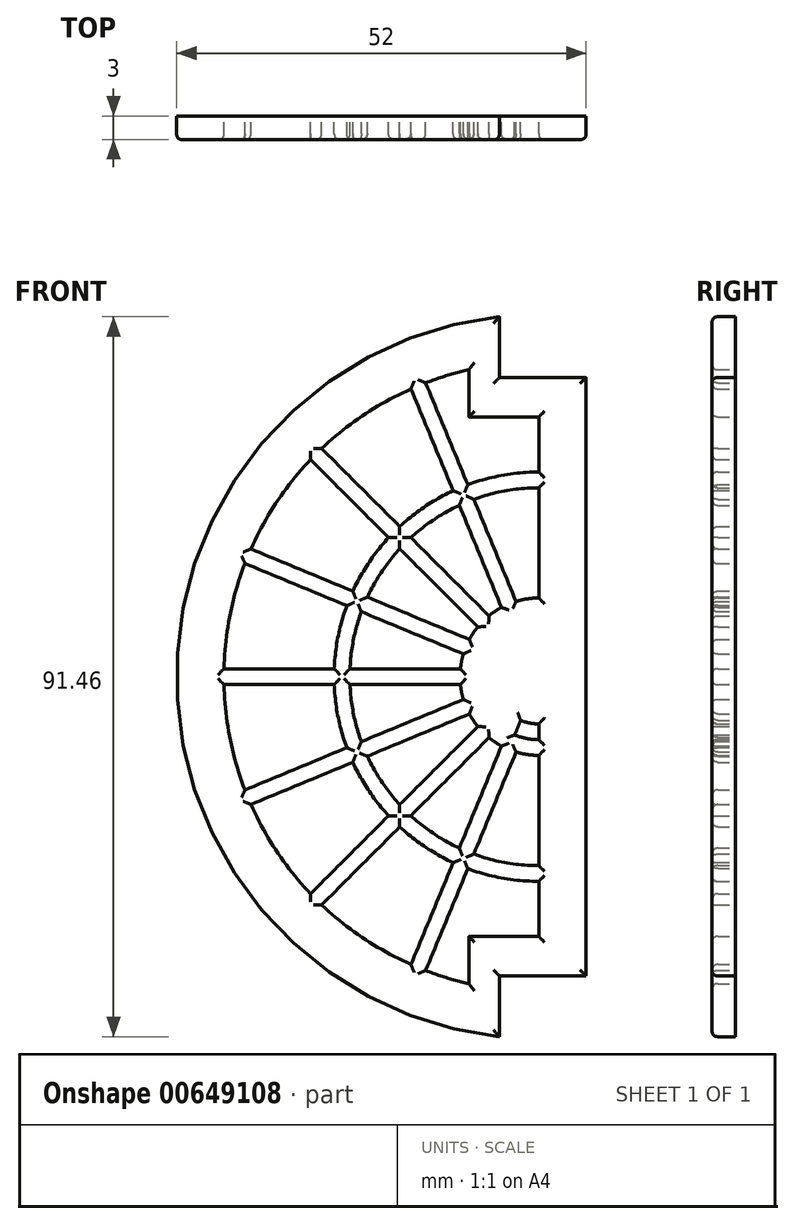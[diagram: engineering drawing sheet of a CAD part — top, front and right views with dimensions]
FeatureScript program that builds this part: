
annotation { "Feature Type Name" : "Feature", "Feature Type Description" : "" }
export const myFeature = defineFeature(function(context is Context, id is Id, definition is map)
    precondition{}
    {
        {
            var Q0;
            Q0=qCreatedBy(makeId("Front.planeOp"),FACE);
            var sketch = newSketch(context, id + "F0", { "sketchPlane" : qUnion([Q0])});
            skPoint(sketch, "E0", {"position": v(0, 0) * mm});
            skPoint(sketch, "E1", {"position": v(-24, 0) * mm});
            skPoint(sketch, "E2", {"position": v(-26, 0) * mm});
            skPoint(sketch, "E3", {"position": v(-28.28, 28.28) * mm});
            skPoint(sketch, "E4", {"position": v(-36.96, 15.3) * mm});
            skPoint(sketch, "E5", {"position": v(-36.96, -15.3) * mm});
            skPoint(sketch, "E6", {"position": v(-28.28, -28.28) * mm});
            skPoint(sketch, "E7", {"position": v(-15.3, -36.96) * mm});
            skPoint(sketch, "E8", {"position": v(-15.3, 36.96) * mm});
            skPoint(sketch, "E9", {"position": v(0, 26) * mm});
            skPoint(sketch, "E10", {"position": v(-9.95, 24.02) * mm});
            skPoint(sketch, "E11", {"position": v(-18.38, 18.38) * mm});
            skPoint(sketch, "E12", {"position": v(-24.02, 9.95) * mm});
            skPoint(sketch, "E13", {"position": v(-22.17, 9.18) * mm});
            skPoint(sketch, "E14", {"position": v(-16.97, 16.97) * mm});
            skPoint(sketch, "E15", {"position": v(-9.18, 22.17) * mm});
            skPoint(sketch, "E16", {"position": v(0, 24) * mm});
            skPoint(sketch, "E17", {"position": v(-22.17, -9.18) * mm});
            skPoint(sketch, "E18", {"position": v(-24.02, -9.95) * mm});
            skPoint(sketch, "E19", {"position": v(-16.97, -16.97) * mm});
            skPoint(sketch, "E20", {"position": v(-18.38, -18.38) * mm});
            skPoint(sketch, "E21", {"position": v(-9.18, -22.17) * mm});
            skPoint(sketch, "E22", {"position": v(-9.95, -24.02) * mm});
            skPoint(sketch, "E23", {"position": v(0, -24) * mm});
            skPoint(sketch, "E24", {"position": v(0, -26) * mm});
            skPoint(sketch, "E25", {"position": v(-40, 0) * mm});
            skPoint(sketch, "E26", {"position": v(6, -38) * mm});
            skLineSegment(sketch, "E27", {"start": v(-5, -38) * mm, "end": v(-5, -45.73) * mm});
            skLineSegment(sketch, "E28", {"start": v(-15.3, 36.96) * mm, "end": v(-9.95, 24.02) * mm});
            skLineSegment(sketch, "E29", {"start": v(-9.18, 22.17) * mm, "end": v(0, 0) * mm});
            skLineSegment(sketch, "E30", {"start": v(-28.28, 28.28) * mm, "end": v(-18.38, 18.38) * mm});
            skLineSegment(sketch, "E31", {"start": v(-16.97, 16.97) * mm, "end": v(0, 0) * mm});
            skLineSegment(sketch, "E32", {"start": v(-36.96, 15.3) * mm, "end": v(-24.02, 9.95) * mm});
            skLineSegment(sketch, "E33", {"start": v(-22.17, 9.18) * mm, "end": v(0, 0) * mm});
            skLineSegment(sketch, "E34", {"start": v(-40, 0) * mm, "end": v(-26, 0) * mm});
            skLineSegment(sketch, "E35", {"start": v(-24, 0) * mm, "end": v(0, 0) * mm});
            skLineSegment(sketch, "E36", {"start": v(-36.96, -15.3) * mm, "end": v(-24.02, -9.95) * mm});
            skLineSegment(sketch, "E37", {"start": v(-22.17, -9.18) * mm, "end": v(0, 0) * mm});
            skLineSegment(sketch, "E38", {"start": v(-28.28, -28.28) * mm, "end": v(-18.38, -18.38) * mm});
            skLineSegment(sketch, "E39", {"start": v(-16.97, -16.97) * mm, "end": v(0, 0) * mm});
            skLineSegment(sketch, "E40", {"start": v(-15.3, -36.96) * mm, "end": v(-9.95, -24.02) * mm});
            skLineSegment(sketch, "E41", {"start": v(-9.18, -22.17) * mm, "end": v(0, 0) * mm});
            skArc(sketch, "E42", {"start": v(-46, 0) * mm, "mid": v(-34.25, -30.7) * mm, "end": v(-5, -45.73) * mm});
            skArc(sketch, "E43", {"start": v(0, 26) * mm, "mid": v(-18.38, 18.38) * mm, "end": v(-26, 0) * mm});
            skArc(sketch, "E44", {"start": v(-26, 0) * mm, "mid": v(-18.38, -18.38) * mm, "end": v(0, -26) * mm});
            skArc(sketch, "E45", {"start": v(0, 24) * mm, "mid": v(-24, 0) * mm, "end": v(0, -24) * mm});
            skArc(sketch, "E46", {"start": v(0, 10) * mm, "mid": v(-10, 0) * mm, "end": v(0, -10) * mm});
            skArc(sketch, "E47", {"start": v(0, 8) * mm, "mid": v(-8, 0) * mm, "end": v(0, -8) * mm});
            skLineSegment(sketch, "E48", {"start": v(6, 38) * mm, "end": v(6, -38) * mm});
            skLineSegment(sketch, "E49", {"start": v(0, 24) * mm, "end": v(0, 10) * mm});
            skLineSegment(sketch, "E50", {"start": v(0, 8) * mm, "end": v(0, -8) * mm});
            skLineSegment(sketch, "E51", {"start": v(0, -10) * mm, "end": v(0, -24) * mm});
            skLineSegment(sketch, "E52", {"start": v(6, -38) * mm, "end": v(-5, -38) * mm});
            skPoint(sketch, "E53", {"position": v(-5, 45.73) * mm});
            skArc(sketch, "E54", {"start": v(-5, 45.73) * mm, "mid": v(-34.25, 30.7) * mm, "end": v(-46, 0) * mm});
            skLineSegment(sketch, "E55", {"start": v(6, 38) * mm, "end": v(-5, 38) * mm});
            skPoint(sketch, "E56", {"position": v(0, 33) * mm});
            skLineSegment(sketch, "E57", {"start": v(0, 33) * mm, "end": v(-8.89, 33) * mm});
            skPoint(sketch, "E58", {"position": v(-8.89, 39) * mm});
            skArc(sketch, "E59", {"start": v(-8.89, 39) * mm, "mid": v(-31.27, 24.94) * mm, "end": v(-40, 0) * mm});
            skLineSegment(sketch, "E60", {"start": v(0, 33) * mm, "end": v(0, 26) * mm});
            skPoint(sketch, "E61", {"position": v(-5, -45.73) * mm});
            skLineSegment(sketch, "E62", {"start": v(-8.89, -33) * mm, "end": v(0, -33) * mm});
            skLineSegment(sketch, "E63", {"start": v(0, -26) * mm, "end": v(0, -33) * mm});
            skPoint(sketch, "E64", {"position": v(-8.89, -39) * mm});
            skPoint(sketch, "E65", {"position": v(-8.89, -33) * mm});
            skArc(sketch, "E66", {"start": v(-40, 0) * mm, "mid": v(-31.27, -24.94) * mm, "end": v(-8.89, -39) * mm});
            skLineSegment(sketch, "E67", {"start": v(-8.89, -33) * mm, "end": v(-8.89, -39) * mm});
            skLineSegment(sketch, "E68", {"start": v(-8.89, 39) * mm, "end": v(-8.89, 33) * mm});
            skLineSegment(sketch, "E69", {"start": v(-5, 45.73) * mm, "end": v(-5, 38) * mm});
            skLineSegment(sketch, "E70.0", {"start": v(-39.99, -1) * mm, "end": v(-25.98, -1) * mm});
            skLineSegment(sketch, "E71.0", {"start": v(-39.99, 1) * mm, "end": v(-25.98, 1) * mm});
            skLineSegment(sketch, "E72", {"start": v(-23.98, -1) * mm, "end": v(-9.95, -1) * mm});
            skLineSegment(sketch, "E73", {"start": v(-23.98, 1) * mm, "end": v(-9.95, 1) * mm});
            skLineSegment(sketch, "E74.0", {"start": v(-36.56, -16.23) * mm, "end": v(-23.62, -10.87) * mm});
            skLineSegment(sketch, "E75.0", {"start": v(-37.33, -14.38) * mm, "end": v(-24.39, -9.02) * mm});
            skPoint(sketch, "E76", {"position": v(-21.77, 10.1) * mm});
            skPoint(sketch, "E77", {"position": v(-8.8, 4.73) * mm});
            skPoint(sketch, "E78", {"position": v(-9.58, 2.88) * mm});
            skPoint(sketch, "E79", {"position": v(-22.54, 8.25) * mm});
            skLineSegment(sketch, "E80", {"start": v(-8.8, 4.73) * mm, "end": v(-21.77, 10.1) * mm});
            skLineSegment(sketch, "E81", {"start": v(-9.58, 2.88) * mm, "end": v(-22.54, 8.25) * mm});
            skPoint(sketch, "E82", {"position": v(-9.57, -2.88) * mm});
            skPoint(sketch, "E83", {"position": v(-9.24, -3.83) * mm});
            skPoint(sketch, "E84", {"position": v(-7.07, -7.07) * mm});
            skPoint(sketch, "E85", {"position": v(-7.74, -6.33) * mm});
            skPoint(sketch, "E86", {"position": v(-6.33, -7.74) * mm});
            skPoint(sketch, "E87", {"position": v(-4.73, -8.8) * mm});
            skPoint(sketch, "E88", {"position": v(-2.88, -9.58) * mm});
            skPoint(sketch, "E89", {"position": v(-7.07, 7.07) * mm});
            skPoint(sketch, "E90", {"position": v(-7.74, 6.33) * mm});
            skPoint(sketch, "E91", {"position": v(-6.33, 7.74) * mm});
            skPoint(sketch, "E92", {"position": v(-4.73, 8.8) * mm});
            skPoint(sketch, "E93", {"position": v(-2.88, 9.57) * mm});
            skPoint(sketch, "E94", {"position": v(-22.54, -8.25) * mm});
            skPoint(sketch, "E95", {"position": v(-17.66, -16.25) * mm});
            skPoint(sketch, "E96", {"position": v(-16.25, -17.66) * mm});
            skPoint(sketch, "E97", {"position": v(-10.1, -21.77) * mm});
            skPoint(sketch, "E98", {"position": v(-8.25, -22.54) * mm});
            skPoint(sketch, "E99", {"position": v(-14.38, -37.33) * mm});
            skPoint(sketch, "E100", {"position": v(-27.57, -28.98) * mm});
            skPoint(sketch, "E101", {"position": v(-28.98, -27.57) * mm});
            skPoint(sketch, "E102", {"position": v(-23.62, 10.87) * mm});
            skPoint(sketch, "E103", {"position": v(-24.39, 9.02) * mm});
            skPoint(sketch, "E104", {"position": v(-36.56, 16.23) * mm});
            skPoint(sketch, "E105", {"position": v(-37.33, 14.38) * mm});
            skPoint(sketch, "E106", {"position": v(-19.08, 17.66) * mm});
            skPoint(sketch, "E107", {"position": v(-8.25, 22.54) * mm});
            skPoint(sketch, "E108", {"position": v(-10.1, 21.77) * mm});
            skPoint(sketch, "E109", {"position": v(-10.87, 23.62) * mm});
            skPoint(sketch, "E110", {"position": v(-14.38, 37.33) * mm});
            skPoint(sketch, "E111", {"position": v(-16.23, 36.56) * mm});
            skPoint(sketch, "E112", {"position": v(-27.57, 28.98) * mm});
            skPoint(sketch, "E113", {"position": v(-28.98, 27.57) * mm});
            skLineSegment(sketch, "E114", {"start": v(-16.23, 36.56) * mm, "end": v(-10.87, 23.62) * mm});
            skLineSegment(sketch, "E115", {"start": v(-28.98, 27.57) * mm, "end": v(-19.08, 17.66) * mm});
            skLineSegment(sketch, "E116", {"start": v(-36.56, 16.23) * mm, "end": v(-23.62, 10.87) * mm});
            skLineSegment(sketch, "E117", {"start": v(-37.33, 14.38) * mm, "end": v(-24.39, 9.02) * mm});
            skLineSegment(sketch, "E118", {"start": v(-8.25, 22.54) * mm, "end": v(-2.88, 9.57) * mm});
            skLineSegment(sketch, "E119", {"start": v(-10.1, 21.77) * mm, "end": v(-4.73, 8.8) * mm});
            skLineSegment(sketch, "E120", {"start": v(-9.57, -2.88) * mm, "end": v(-22.54, -8.25) * mm});
            skLineSegment(sketch, "E121", {"start": v(-2.88, -9.58) * mm, "end": v(-8.25, -22.54) * mm});
            skLineSegment(sketch, "E122", {"start": v(-4.73, -8.8) * mm, "end": v(-10.1, -21.77) * mm});
            skLineSegment(sketch, "E123", {"start": v(-6.33, -7.74) * mm, "end": v(-16.25, -17.66) * mm});
            skLineSegment(sketch, "E124", {"start": v(-7.74, -6.33) * mm, "end": v(-17.66, -16.25) * mm});
            skPoint(sketch, "E125", {"position": v(-8.81, -4.73) * mm});
            skPoint(sketch, "E126", {"position": v(-17.66, -19.08) * mm});
            skPoint(sketch, "E127", {"position": v(-19.08, -17.66) * mm});
            skLineSegment(sketch, "E128", {"start": v(-19.08, -17.66) * mm, "end": v(-28.98, -27.57) * mm});
            skLineSegment(sketch, "E129", {"start": v(-17.66, -19.08) * mm, "end": v(-27.57, -28.98) * mm});
            skPoint(sketch, "E130", {"position": v(-3.83, 9.24) * mm});
            skPoint(sketch, "E131", {"position": v(-9.02, -24.39) * mm});
            skLineSegment(sketch, "E132", {"start": v(-9.02, -24.39) * mm, "end": v(-14.38, -37.33) * mm});
            skPoint(sketch, "E133", {"position": v(-9.02, 24.39) * mm});
            skLineSegment(sketch, "E134", {"start": v(-14.38, 37.33) * mm, "end": v(-9.02, 24.39) * mm});
            skPoint(sketch, "E135", {"position": v(-17.66, 19.08) * mm});
            skLineSegment(sketch, "E136", {"start": v(-17.66, 19.08) * mm, "end": v(-27.57, 28.98) * mm});
            skPoint(sketch, "E137", {"position": v(-16.25, 17.66) * mm});
            skPoint(sketch, "E138", {"position": v(-17.66, 16.25) * mm});
            skLineSegment(sketch, "E139", {"start": v(-16.25, 17.66) * mm, "end": v(-6.33, 7.74) * mm});
            skLineSegment(sketch, "E140", {"start": v(-17.66, 16.25) * mm, "end": v(-7.74, 6.33) * mm});
            skPoint(sketch, "E141", {"position": v(-21.77, -10.1) * mm});
            skLineSegment(sketch, "E142", {"start": v(-8.81, -4.73) * mm, "end": v(-21.77, -10.1) * mm});
            skPoint(sketch, "E143", {"position": v(-16.23, -36.56) * mm});
            skPoint(sketch, "E144", {"position": v(-10.87, -23.62) * mm});
            skLineSegment(sketch, "E145", {"start": v(-10.87, -23.62) * mm, "end": v(-16.23, -36.56) * mm});
            skPoint(sketch, "E146", {"position": v(0, 6) * mm});
            skPoint(sketch, "E147", {"position": v(0, -6) * mm});
            skPoint(sketch, "E148", {"position": v(-6, 0) * mm});
            skArc(sketch, "E149", {"start": v(0, 6) * mm, "mid": v(-6, 0) * mm, "end": v(0, -6) * mm});
            skPoint(sketch, "E150", {"position": v(0, 4) * mm});
            skPoint(sketch, "E151", {"position": v(0, -4) * mm});
            skArc(sketch, "E152", {"start": v(0, 4) * mm, "mid": v(-4, 0) * mm, "end": v(0, -4) * mm});
            skPoint(sketch, "E153", {"position": v(0, 2) * mm});
            skPoint(sketch, "E154", {"position": v(0, -2) * mm});
            skPoint(sketch, "E155", {"position": v(4.5, 0) * mm});
            skPoint(sketch, "E156", {"position": v(3, 0) * mm});
            skPoint(sketch, "E157", {"position": v(6, 8.02) * mm});
            skPoint(sketch, "E158", {"position": v(6, -5.97) * mm});
            skPoint(sketch, "E159", {"position": v(6, -7.97) * mm});
            skPoint(sketch, "E160", {"position": v(6, -10.01) * mm});
            skPoint(sketch, "E161", {"position": v(5, -10) * mm});
            skPoint(sketch, "E162", {"position": v(3, 10.03) * mm});
            skPoint(sketch, "E163", {"position": v(6, 6.02) * mm});
            skPoint(sketch, "E164", {"position": v(6, 4.02) * mm});
            skPoint(sketch, "E165", {"position": v(6, 2.04) * mm});
            skPoint(sketch, "E166", {"position": v(6, -3.96) * mm});
            skPoint(sketch, "E167", {"position": v(2, 10.02) * mm});
            skPoint(sketch, "E168", {"position": v(5, 10.01) * mm});
            skPoint(sketch, "E169", {"position": v(6, 10.01) * mm});
            skPoint(sketch, "E170", {"position": v(4, 10.01) * mm});
            skPoint(sketch, "E171", {"position": v(6, -1.99) * mm});
            skLineSegment(sketch, "E172", {"start": v(5, 10.01) * mm, "end": v(5, -10) * mm});
            skLineSegment(sketch, "E173", {"start": v(4, 8) * mm, "end": v(0, 8) * mm});
            skLineSegment(sketch, "E174", {"start": v(3, 6) * mm, "end": v(0, 6) * mm});
            skLineSegment(sketch, "E175", {"start": v(2, 4) * mm, "end": v(0, 4) * mm});
            skPoint(sketch, "E176", {"position": v(1, -2) * mm});
            skPoint(sketch, "E177", {"position": v(3, -5.98) * mm});
            skPoint(sketch, "E178", {"position": v(4, -7.98) * mm});
            skPoint(sketch, "E179", {"position": v(5, 8) * mm});
            skPoint(sketch, "E180", {"position": v(3, 8) * mm});
            skPoint(sketch, "E181", {"position": v(2, 8) * mm});
            skPoint(sketch, "E182", {"position": v(1, 8) * mm});
            skPoint(sketch, "E183", {"position": v(1, 6) * mm});
            skPoint(sketch, "E184", {"position": v(2, 6) * mm});
            skPoint(sketch, "E185", {"position": v(4, 6) * mm});
            skPoint(sketch, "E186", {"position": v(3, 4.02) * mm});
            skPoint(sketch, "E187", {"position": v(4, 4.02) * mm});
            skPoint(sketch, "E188", {"position": v(4, 2) * mm});
            skPoint(sketch, "E189", {"position": v(2, 2) * mm});
            skPoint(sketch, "E190", {"position": v(1, 2) * mm});
            skPoint(sketch, "E191", {"position": v(2, -1.99) * mm});
            skPoint(sketch, "E192", {"position": v(3, -1.99) * mm});
            skPoint(sketch, "E193", {"position": v(4, -1.99) * mm});
            skPoint(sketch, "E194", {"position": v(3, -4) * mm});
            skPoint(sketch, "E195", {"position": v(4, -3.99) * mm});
            skLineSegment(sketch, "E196", {"start": v(0, 2) * mm, "end": v(1, 2) * mm});
            skLineSegment(sketch, "E197", {"start": v(1, -2) * mm, "end": v(1, 2) * mm});
            skLineSegment(sketch, "E198", {"start": v(1, -2) * mm, "end": v(0, -2) * mm});
            skPoint(sketch, "E199", {"position": v(2, -4) * mm});
            skLineSegment(sketch, "E200", {"start": v(2, 4) * mm, "end": v(2, -4) * mm});
            skLineSegment(sketch, "E201", {"start": v(2, -4) * mm, "end": v(0, -4) * mm});
            skLineSegment(sketch, "E202", {"start": v(3, 6) * mm, "end": v(3, -5.98) * mm});
            skLineSegment(sketch, "E203", {"start": v(4, -7.98) * mm, "end": v(0, -8) * mm});
            skLineSegment(sketch, "E204", {"start": v(3, -5.98) * mm, "end": v(0, -6) * mm});
            skLineSegment(sketch, "E205", {"start": v(5, -10) * mm, "end": v(0, -10) * mm});
            skLineSegment(sketch, "E206", {"start": v(4, 8) * mm, "end": v(4, -7.98) * mm});
            skArc(sketch, "E207", {"start": v(0, -8) * mm, "mid": v(-1.56, -7.85) * mm, "end": v(-3.06, -7.4) * mm});
            skArc(sketch, "E208", {"start": v(0, 2) * mm, "mid": v(-2, 0) * mm, "end": v(0, -2) * mm});
            skSolve(sketch);
        }
        {
            var Q0;
            {var subQ0=sQuery(id+"F0.wireOp",EDGE,"E46");var subQ3=sQuery(id+"F0.wireOp",EDGE,"E29");var subQ4=makeQuery(id+"F0.imprint","INTERSECT",VERTEX,{"derivedFrom":[subQ3,subQ0]});Q0=makeQuery(id+"F0.imprint","IMPRINT",FACE,{"disambiguationData":[TD([[makeQuery(id+"F0.imprint","IMPRINT",EDGE,{"disambiguationData":[TD([[subQ4,-1.0]])],"derivedFrom":subQ3}),-1.0]])]});}
            var Q1;
            {var subQ0=sQuery(id+"F0.wireOp",EDGE,"E46");var subQ2=sQuery(id+"F0.wireOp",EDGE,"E35");var subQ3=makeQuery(id+"F0.imprint","INTERSECT",VERTEX,{"derivedFrom":[subQ2,subQ0]});Q1=makeQuery(id+"F0.imprint","IMPRINT",FACE,{"disambiguationData":[TD([[makeQuery(id+"F0.imprint","IMPRINT",EDGE,{"disambiguationData":[TD([[subQ3,-1.0]])],"derivedFrom":subQ2}),-1.0]])]});}
            var Q2;
            {var subQ0=sQuery(id+"F0.wireOp",EDGE,"E46");var subQ3=sQuery(id+"F0.wireOp",EDGE,"E39");var subQ4=makeQuery(id+"F0.imprint","INTERSECT",VERTEX,{"derivedFrom":[subQ3,subQ0]});Q2=makeQuery(id+"F0.imprint","IMPRINT",FACE,{"disambiguationData":[TD([[makeQuery(id+"F0.imprint","IMPRINT",EDGE,{"disambiguationData":[TD([[subQ4,-1.0]])],"derivedFrom":subQ3}),-1.0]])]});}
            var Q3;
            {var subQ0=sQuery(id+"F0.wireOp",EDGE,"E149");var subQ1=sQuery(id+"F0.wireOp",EDGE,"E31");var subQ2=makeQuery(id+"F0.imprint","INTERSECT",VERTEX,{"derivedFrom":[subQ1,subQ0]});Q3=makeQuery(id+"F0.imprint","IMPRINT",FACE,{"disambiguationData":[TD([[makeQuery(id+"F0.imprint","IMPRINT",EDGE,{"disambiguationData":[TD([[subQ2,-1.0]])],"derivedFrom":subQ1}),-1.0]])]});}
            var Q4;
            {var subQ0=sQuery(id+"F0.wireOp",EDGE,"E149");var subQ1=sQuery(id+"F0.wireOp",EDGE,"E33");var subQ2=makeQuery(id+"F0.imprint","INTERSECT",VERTEX,{"derivedFrom":[subQ1,subQ0]});Q4=makeQuery(id+"F0.imprint","IMPRINT",FACE,{"disambiguationData":[TD([[makeQuery(id+"F0.imprint","IMPRINT",EDGE,{"disambiguationData":[TD([[subQ2,-1.0]])],"derivedFrom":subQ1}),-1.0]])]});}
            var Q5;
            {var subQ0=sQuery(id+"F0.wireOp",EDGE,"E149");var subQ1=sQuery(id+"F0.wireOp",EDGE,"E35");var subQ2=makeQuery(id+"F0.imprint","INTERSECT",VERTEX,{"derivedFrom":[subQ1,subQ0]});Q5=makeQuery(id+"F0.imprint","IMPRINT",FACE,{"disambiguationData":[TD([[makeQuery(id+"F0.imprint","IMPRINT",EDGE,{"disambiguationData":[TD([[subQ2,-1.0]])],"derivedFrom":subQ1}),-1.0]])]});}
            var Q6;
            {var subQ0=sQuery(id+"F0.wireOp",EDGE,"E149");var subQ1=sQuery(id+"F0.wireOp",EDGE,"E37");var subQ2=makeQuery(id+"F0.imprint","INTERSECT",VERTEX,{"derivedFrom":[subQ1,subQ0]});Q6=makeQuery(id+"F0.imprint","IMPRINT",FACE,{"disambiguationData":[TD([[makeQuery(id+"F0.imprint","IMPRINT",EDGE,{"disambiguationData":[TD([[subQ2,-1.0]])],"derivedFrom":subQ1}),-1.0]])]});}
            var Q7;
            {var subQ0=sQuery(id+"F0.wireOp",EDGE,"E149");var subQ1=sQuery(id+"F0.wireOp",EDGE,"E39");var subQ2=makeQuery(id+"F0.imprint","INTERSECT",VERTEX,{"derivedFrom":[subQ1,subQ0]});Q7=makeQuery(id+"F0.imprint","IMPRINT",FACE,{"disambiguationData":[TD([[makeQuery(id+"F0.imprint","IMPRINT",EDGE,{"disambiguationData":[TD([[subQ2,-1.0]])],"derivedFrom":subQ1}),-1.0]])]});}
            var Q8;
            {var subQ0=sQuery(id+"F0.wireOp",EDGE,"E149");var subQ1=sQuery(id+"F0.wireOp",EDGE,"E41");var subQ2=makeQuery(id+"F0.imprint","INTERSECT",VERTEX,{"derivedFrom":[subQ1,subQ0]});Q8=makeQuery(id+"F0.imprint","IMPRINT",FACE,{"disambiguationData":[TD([[makeQuery(id+"F0.imprint","IMPRINT",EDGE,{"disambiguationData":[TD([[subQ2,-1.0]])],"derivedFrom":subQ1}),-1.0]])]});}
            var Q9;
            Q9=makeQuery(id+"F0.imprint","IMPRINT",FACE,{"disambiguationData":[TD([[makeQuery(id+"F0.imprint","IMPRINT",EDGE,{"derivedFrom":sQuery(id+"F0.wireOp",EDGE,"E27")}),-1.0]])]});
            var Q10;
            {var subQ5=sQuery(id+"F0.wireOp",EDGE,"E118");Q10=makeQuery(id+"F0.imprint","IMPRINT",FACE,{"disambiguationData":[TD([[makeQuery(id+"F0.imprint","IMPRINT",EDGE,{"derivedFrom":subQ5}),-1.0]])]});}
            var Q11;
            {var subQ5=sQuery(id+"F0.wireOp",EDGE,"E119");Q11=makeQuery(id+"F0.imprint","IMPRINT",FACE,{"disambiguationData":[TD([[makeQuery(id+"F0.imprint","IMPRINT",EDGE,{"derivedFrom":subQ5}),1.0]])]});}
            var Q12;
            {var subQ5=sQuery(id+"F0.wireOp",EDGE,"E139");Q12=makeQuery(id+"F0.imprint","IMPRINT",FACE,{"disambiguationData":[TD([[makeQuery(id+"F0.imprint","IMPRINT",EDGE,{"derivedFrom":subQ5}),-1.0]])]});}
            var Q13;
            {var subQ5=sQuery(id+"F0.wireOp",EDGE,"E140");Q13=makeQuery(id+"F0.imprint","IMPRINT",FACE,{"disambiguationData":[TD([[makeQuery(id+"F0.imprint","IMPRINT",EDGE,{"derivedFrom":subQ5}),1.0]])]});}
            var Q14;
            {var subQ0=sQuery(id+"F0.wireOp",EDGE,"E28");Q14=makeQuery(id+"F0.imprint","IMPRINT",FACE,{"disambiguationData":[TD([[makeQuery(id+"F0.imprint","IMPRINT",EDGE,{"derivedFrom":subQ0}),1.0]])]});}
            var Q15;
            {var subQ0=sQuery(id+"F0.wireOp",EDGE,"E28");Q15=makeQuery(id+"F0.imprint","IMPRINT",FACE,{"disambiguationData":[TD([[makeQuery(id+"F0.imprint","IMPRINT",EDGE,{"derivedFrom":subQ0}),-1.0]])]});}
            var Q16;
            {var subQ0=sQuery(id+"F0.wireOp",EDGE,"E30");Q16=makeQuery(id+"F0.imprint","IMPRINT",FACE,{"disambiguationData":[TD([[makeQuery(id+"F0.imprint","IMPRINT",EDGE,{"derivedFrom":subQ0}),1.0]])]});}
            var Q17;
            {var subQ0=sQuery(id+"F0.wireOp",EDGE,"E30");Q17=makeQuery(id+"F0.imprint","IMPRINT",FACE,{"disambiguationData":[TD([[makeQuery(id+"F0.imprint","IMPRINT",EDGE,{"derivedFrom":subQ0}),-1.0]])]});}
            var Q18;
            {var subQ0=sQuery(id+"F0.wireOp",EDGE,"E32");Q18=makeQuery(id+"F0.imprint","IMPRINT",FACE,{"disambiguationData":[TD([[makeQuery(id+"F0.imprint","IMPRINT",EDGE,{"derivedFrom":subQ0}),1.0]])]});}
            var Q19;
            {var subQ5=sQuery(id+"F0.wireOp",EDGE,"E80");Q19=makeQuery(id+"F0.imprint","IMPRINT",FACE,{"disambiguationData":[TD([[makeQuery(id+"F0.imprint","IMPRINT",EDGE,{"derivedFrom":subQ5}),1.0]])]});}
            var Q20;
            {var subQ5=sQuery(id+"F0.wireOp",EDGE,"E81");Q20=makeQuery(id+"F0.imprint","IMPRINT",FACE,{"disambiguationData":[TD([[makeQuery(id+"F0.imprint","IMPRINT",EDGE,{"derivedFrom":subQ5}),-1.0]])]});}
            var Q21;
            {var subQ0=sQuery(id+"F0.wireOp",EDGE,"E32");Q21=makeQuery(id+"F0.imprint","IMPRINT",FACE,{"disambiguationData":[TD([[makeQuery(id+"F0.imprint","IMPRINT",EDGE,{"derivedFrom":subQ0}),-1.0]])]});}
            var Q22;
            {var subQ0=sQuery(id+"F0.wireOp",EDGE,"E34");Q22=makeQuery(id+"F0.imprint","IMPRINT",FACE,{"disambiguationData":[TD([[makeQuery(id+"F0.imprint","IMPRINT",EDGE,{"derivedFrom":subQ0}),1.0]])]});}
            var Q23;
            {var subQ0=sQuery(id+"F0.wireOp",EDGE,"E34");Q23=makeQuery(id+"F0.imprint","IMPRINT",FACE,{"disambiguationData":[TD([[makeQuery(id+"F0.imprint","IMPRINT",EDGE,{"derivedFrom":subQ0}),-1.0]])]});}
            var Q24;
            {var subQ5=sQuery(id+"F0.wireOp",EDGE,"E73");Q24=makeQuery(id+"F0.imprint","IMPRINT",FACE,{"disambiguationData":[TD([[makeQuery(id+"F0.imprint","IMPRINT",EDGE,{"derivedFrom":subQ5}),-1.0]])]});}
            var Q25;
            {var subQ5=sQuery(id+"F0.wireOp",EDGE,"E72");Q25=makeQuery(id+"F0.imprint","IMPRINT",FACE,{"disambiguationData":[TD([[makeQuery(id+"F0.imprint","IMPRINT",EDGE,{"derivedFrom":subQ5}),1.0]])]});}
            var Q26;
            {var subQ5=sQuery(id+"F0.wireOp",EDGE,"E120");Q26=makeQuery(id+"F0.imprint","IMPRINT",FACE,{"disambiguationData":[TD([[makeQuery(id+"F0.imprint","IMPRINT",EDGE,{"derivedFrom":subQ5}),1.0]])]});}
            var Q27;
            {var subQ0=sQuery(id+"F0.wireOp",EDGE,"E36");Q27=makeQuery(id+"F0.imprint","IMPRINT",FACE,{"disambiguationData":[TD([[makeQuery(id+"F0.imprint","IMPRINT",EDGE,{"derivedFrom":subQ0}),1.0]])]});}
            var Q28;
            {var subQ5=sQuery(id+"F0.wireOp",EDGE,"E142");Q28=makeQuery(id+"F0.imprint","IMPRINT",FACE,{"disambiguationData":[TD([[makeQuery(id+"F0.imprint","IMPRINT",EDGE,{"derivedFrom":subQ5}),-1.0]])]});}
            var Q29;
            {var subQ0=sQuery(id+"F0.wireOp",EDGE,"E36");Q29=makeQuery(id+"F0.imprint","IMPRINT",FACE,{"disambiguationData":[TD([[makeQuery(id+"F0.imprint","IMPRINT",EDGE,{"derivedFrom":subQ0}),-1.0]])]});}
            var Q30;
            {var subQ5=sQuery(id+"F0.wireOp",EDGE,"E124");Q30=makeQuery(id+"F0.imprint","IMPRINT",FACE,{"disambiguationData":[TD([[makeQuery(id+"F0.imprint","IMPRINT",EDGE,{"derivedFrom":subQ5}),1.0]])]});}
            var Q31;
            {var subQ0=sQuery(id+"F0.wireOp",EDGE,"E38");Q31=makeQuery(id+"F0.imprint","IMPRINT",FACE,{"disambiguationData":[TD([[makeQuery(id+"F0.imprint","IMPRINT",EDGE,{"derivedFrom":subQ0}),1.0]])]});}
            var Q32;
            {var subQ5=sQuery(id+"F0.wireOp",EDGE,"E123");Q32=makeQuery(id+"F0.imprint","IMPRINT",FACE,{"disambiguationData":[TD([[makeQuery(id+"F0.imprint","IMPRINT",EDGE,{"derivedFrom":subQ5}),-1.0]])]});}
            var Q33;
            {var subQ0=sQuery(id+"F0.wireOp",EDGE,"E38");Q33=makeQuery(id+"F0.imprint","IMPRINT",FACE,{"disambiguationData":[TD([[makeQuery(id+"F0.imprint","IMPRINT",EDGE,{"derivedFrom":subQ0}),-1.0]])]});}
            var Q34;
            {var subQ5=sQuery(id+"F0.wireOp",EDGE,"E121");Q34=makeQuery(id+"F0.imprint","IMPRINT",FACE,{"disambiguationData":[TD([[makeQuery(id+"F0.imprint","IMPRINT",EDGE,{"derivedFrom":subQ5}),-1.0]])]});}
            var Q35;
            {var subQ0=sQuery(id+"F0.wireOp",EDGE,"E40");Q35=makeQuery(id+"F0.imprint","IMPRINT",FACE,{"disambiguationData":[TD([[makeQuery(id+"F0.imprint","IMPRINT",EDGE,{"derivedFrom":subQ0}),1.0]])]});}
            var Q36;
            {var subQ5=sQuery(id+"F0.wireOp",EDGE,"E122");Q36=makeQuery(id+"F0.imprint","IMPRINT",FACE,{"disambiguationData":[TD([[makeQuery(id+"F0.imprint","IMPRINT",EDGE,{"derivedFrom":subQ5}),1.0]])]});}
            var Q37;
            {var subQ0=sQuery(id+"F0.wireOp",EDGE,"E40");Q37=makeQuery(id+"F0.imprint","IMPRINT",FACE,{"disambiguationData":[TD([[makeQuery(id+"F0.imprint","IMPRINT",EDGE,{"derivedFrom":subQ0}),-1.0]])]});}
            var Q38;
            {var subQ1=sQuery(id+"F0.wireOp",EDGE,"E29");var subQ3=sQuery(id+"F0.wireOp",EDGE,"E208");var subQ4=makeQuery(id+"F0.imprint","INTERSECT",VERTEX,{"derivedFrom":[subQ1,subQ3]});Q38=makeQuery(id+"F0.imprint","IMPRINT",FACE,{"disambiguationData":[TD([[makeQuery(id+"F0.imprint","IMPRINT",EDGE,{"disambiguationData":[TD([[subQ4,1.0]])],"derivedFrom":subQ3}),1.0]])]});}
            var Q39;
            {var subQ1=sQuery(id+"F0.wireOp",EDGE,"E31");var subQ3=sQuery(id+"F0.wireOp",EDGE,"E208");var subQ4=makeQuery(id+"F0.imprint","INTERSECT",VERTEX,{"derivedFrom":[subQ1,subQ3]});Q39=makeQuery(id+"F0.imprint","IMPRINT",FACE,{"disambiguationData":[TD([[makeQuery(id+"F0.imprint","IMPRINT",EDGE,{"disambiguationData":[TD([[subQ4,-1.0]])],"derivedFrom":subQ3}),1.0]])]});}
            var Q40;
            {var subQ1=sQuery(id+"F0.wireOp",EDGE,"E35");var subQ3=sQuery(id+"F0.wireOp",EDGE,"E208");var subQ4=makeQuery(id+"F0.imprint","INTERSECT",VERTEX,{"derivedFrom":[subQ1,subQ3]});Q40=makeQuery(id+"F0.imprint","IMPRINT",FACE,{"disambiguationData":[TD([[makeQuery(id+"F0.imprint","IMPRINT",EDGE,{"disambiguationData":[TD([[subQ4,-1.0]])],"derivedFrom":subQ3}),1.0]])]});}
            var Q41;
            {var subQ1=sQuery(id+"F0.wireOp",EDGE,"E37");var subQ3=sQuery(id+"F0.wireOp",EDGE,"E208");var subQ4=makeQuery(id+"F0.imprint","INTERSECT",VERTEX,{"derivedFrom":[subQ1,subQ3]});Q41=makeQuery(id+"F0.imprint","IMPRINT",FACE,{"disambiguationData":[TD([[makeQuery(id+"F0.imprint","IMPRINT",EDGE,{"disambiguationData":[TD([[subQ4,-1.0]])],"derivedFrom":subQ3}),1.0]])]});}
            var Q42;
            {var subQ1=sQuery(id+"F0.wireOp",EDGE,"E39");var subQ3=sQuery(id+"F0.wireOp",EDGE,"E208");var subQ4=makeQuery(id+"F0.imprint","INTERSECT",VERTEX,{"derivedFrom":[subQ1,subQ3]});Q42=makeQuery(id+"F0.imprint","IMPRINT",FACE,{"disambiguationData":[TD([[makeQuery(id+"F0.imprint","IMPRINT",EDGE,{"disambiguationData":[TD([[subQ4,-1.0]])],"derivedFrom":subQ3}),1.0]])]});}
            var Q43;
            {var subQ1=sQuery(id+"F0.wireOp",EDGE,"E41");var subQ3=sQuery(id+"F0.wireOp",EDGE,"E208");var subQ4=makeQuery(id+"F0.imprint","INTERSECT",VERTEX,{"derivedFrom":[subQ1,subQ3]});Q43=makeQuery(id+"F0.imprint","IMPRINT",FACE,{"disambiguationData":[TD([[makeQuery(id+"F0.imprint","IMPRINT",EDGE,{"disambiguationData":[TD([[subQ4,-1.0]])],"derivedFrom":subQ3}),1.0]])]});}
            var Q44;
            Q44=makeQuery(id+"F0.imprint","IMPRINT",FACE,{"disambiguationData":[TD([[makeQuery(id+"F0.imprint","IMPRINT",EDGE,{"derivedFrom":sQuery(id+"F0.wireOp",EDGE,"E172")}),-1.0]])]});
            var Q45;
            {var subQ1=sQuery(id+"F0.wireOp",EDGE,"E29");var subQ3=sQuery(id+"F0.wireOp",EDGE,"E208");var subQ4=makeQuery(id+"F0.imprint","INTERSECT",VERTEX,{"derivedFrom":[subQ1,subQ3]});Q45=makeQuery(id+"F0.imprint","IMPRINT",FACE,{"disambiguationData":[TD([[makeQuery(id+"F0.imprint","IMPRINT",EDGE,{"disambiguationData":[TD([[subQ4,-1.0]])],"derivedFrom":subQ3}),1.0]])]});}
            var Q46;
            {var subQ0=sQuery(id+"F0.wireOp",EDGE,"E149");var subQ1=sQuery(id+"F0.wireOp",EDGE,"E29");var subQ2=makeQuery(id+"F0.imprint","INTERSECT",VERTEX,{"derivedFrom":[subQ1,subQ0]});Q46=makeQuery(id+"F0.imprint","IMPRINT",FACE,{"disambiguationData":[TD([[makeQuery(id+"F0.imprint","IMPRINT",EDGE,{"disambiguationData":[TD([[subQ2,-1.0]])],"derivedFrom":subQ1}),1.0]])]});}
            var Q47;
            {var subQ1=sQuery(id+"F0.wireOp",EDGE,"E33");var subQ3=sQuery(id+"F0.wireOp",EDGE,"E208");var subQ4=makeQuery(id+"F0.imprint","INTERSECT",VERTEX,{"derivedFrom":[subQ1,subQ3]});Q47=makeQuery(id+"F0.imprint","IMPRINT",FACE,{"disambiguationData":[TD([[makeQuery(id+"F0.imprint","IMPRINT",EDGE,{"disambiguationData":[TD([[subQ4,-1.0]])],"derivedFrom":subQ3}),1.0]])]});}
            var Q48;
            {var subQ4=sQuery(id+"F0.wireOp",EDGE,"E196");Q48=makeQuery(id+"F0.imprint","IMPRINT",FACE,{"disambiguationData":[TD([[makeQuery(id+"F0.imprint","IMPRINT",EDGE,{"derivedFrom":subQ4}),-1.0]])]});}
            var Q49;
            {var subQ0=sQuery(id+"F0.wireOp",EDGE,"E149");var subQ1=sQuery(id+"F0.wireOp",EDGE,"E29");var subQ2=makeQuery(id+"F0.imprint","INTERSECT",VERTEX,{"derivedFrom":[subQ1,subQ0]});Q49=makeQuery(id+"F0.imprint","IMPRINT",FACE,{"disambiguationData":[TD([[makeQuery(id+"F0.imprint","IMPRINT",EDGE,{"disambiguationData":[TD([[subQ2,-1.0]])],"derivedFrom":subQ1}),-1.0]])]});}
            var Q50;
            {var subQ0=sQuery(id+"F0.wireOp",EDGE,"E46");var subQ7=sQuery(id+"F0.wireOp",EDGE,"E31");var subQ8=makeQuery(id+"F0.imprint","INTERSECT",VERTEX,{"derivedFrom":[subQ7,subQ0]});Q50=makeQuery(id+"F0.imprint","IMPRINT",FACE,{"disambiguationData":[TD([[makeQuery(id+"F0.imprint","IMPRINT",EDGE,{"disambiguationData":[TD([[subQ8,-1.0]])],"derivedFrom":subQ7}),-1.0]])]});}
            var Q51;
            {var subQ0=sQuery(id+"F0.wireOp",EDGE,"E152");var subQ1=sQuery(id+"F0.wireOp",EDGE,"E41");var subQ2=makeQuery(id+"F0.imprint","INTERSECT",VERTEX,{"derivedFrom":[subQ1,subQ0]});Q51=makeQuery(id+"F0.imprint","IMPRINT",FACE,{"disambiguationData":[TD([[makeQuery(id+"F0.imprint","IMPRINT",EDGE,{"disambiguationData":[TD([[subQ2,-1.0]])],"derivedFrom":subQ1}),-1.0]])]});}
            var Q52;
            {var subQ0=sQuery(id+"F0.wireOp",EDGE,"E152");var subQ1=sQuery(id+"F0.wireOp",EDGE,"E39");var subQ2=makeQuery(id+"F0.imprint","INTERSECT",VERTEX,{"derivedFrom":[subQ1,subQ0]});Q52=makeQuery(id+"F0.imprint","IMPRINT",FACE,{"disambiguationData":[TD([[makeQuery(id+"F0.imprint","IMPRINT",EDGE,{"disambiguationData":[TD([[subQ2,-1.0]])],"derivedFrom":subQ1}),-1.0]])]});}
            var Q53;
            {var subQ0=sQuery(id+"F0.wireOp",EDGE,"E152");var subQ1=sQuery(id+"F0.wireOp",EDGE,"E35");var subQ2=makeQuery(id+"F0.imprint","INTERSECT",VERTEX,{"derivedFrom":[subQ1,subQ0]});Q53=makeQuery(id+"F0.imprint","IMPRINT",FACE,{"disambiguationData":[TD([[makeQuery(id+"F0.imprint","IMPRINT",EDGE,{"disambiguationData":[TD([[subQ2,-1.0]])],"derivedFrom":subQ1}),-1.0]])]});}
            var Q54;
            {var subQ0=sQuery(id+"F0.wireOp",EDGE,"E152");var subQ1=sQuery(id+"F0.wireOp",EDGE,"E31");var subQ2=makeQuery(id+"F0.imprint","INTERSECT",VERTEX,{"derivedFrom":[subQ1,subQ0]});Q54=makeQuery(id+"F0.imprint","IMPRINT",FACE,{"disambiguationData":[TD([[makeQuery(id+"F0.imprint","IMPRINT",EDGE,{"disambiguationData":[TD([[subQ2,-1.0]])],"derivedFrom":subQ1}),-1.0]])]});}
            var Q55;
            {var subQ0=sQuery(id+"F0.wireOp",EDGE,"E152");var subQ1=sQuery(id+"F0.wireOp",EDGE,"E29");var subQ2=makeQuery(id+"F0.imprint","INTERSECT",VERTEX,{"derivedFrom":[subQ1,subQ0]});Q55=makeQuery(id+"F0.imprint","IMPRINT",FACE,{"disambiguationData":[TD([[makeQuery(id+"F0.imprint","IMPRINT",EDGE,{"disambiguationData":[TD([[subQ2,-1.0]])],"derivedFrom":subQ1}),1.0]])]});}
            var Q56;
            {var subQ0=sQuery(id+"F0.wireOp",EDGE,"E46");var subQ3=sQuery(id+"F0.wireOp",EDGE,"E33");var subQ4=makeQuery(id+"F0.imprint","INTERSECT",VERTEX,{"derivedFrom":[subQ3,subQ0]});Q56=makeQuery(id+"F0.imprint","IMPRINT",FACE,{"disambiguationData":[TD([[makeQuery(id+"F0.imprint","IMPRINT",EDGE,{"disambiguationData":[TD([[subQ4,-1.0]])],"derivedFrom":subQ3}),-1.0]])]});}
            var Q57;
            {var subQ0=sQuery(id+"F0.wireOp",EDGE,"E174");Q57=makeQuery(id+"F0.imprint","IMPRINT",FACE,{"disambiguationData":[TD([[makeQuery(id+"F0.imprint","IMPRINT",EDGE,{"derivedFrom":subQ0}),1.0]])]});}
            var Q58;
            {var subQ0=sQuery(id+"F0.wireOp",EDGE,"E152");var subQ1=sQuery(id+"F0.wireOp",EDGE,"E33");var subQ2=makeQuery(id+"F0.imprint","INTERSECT",VERTEX,{"derivedFrom":[subQ1,subQ0]});Q58=makeQuery(id+"F0.imprint","IMPRINT",FACE,{"disambiguationData":[TD([[makeQuery(id+"F0.imprint","IMPRINT",EDGE,{"disambiguationData":[TD([[subQ2,-1.0]])],"derivedFrom":subQ1}),-1.0]])]});}
            var Q59;
            {var subQ0=sQuery(id+"F0.wireOp",EDGE,"E152");var subQ1=sQuery(id+"F0.wireOp",EDGE,"E29");var subQ2=makeQuery(id+"F0.imprint","INTERSECT",VERTEX,{"derivedFrom":[subQ1,subQ0]});Q59=makeQuery(id+"F0.imprint","IMPRINT",FACE,{"disambiguationData":[TD([[makeQuery(id+"F0.imprint","IMPRINT",EDGE,{"disambiguationData":[TD([[subQ2,-1.0]])],"derivedFrom":subQ1}),-1.0]])]});}
            var Q60;
            {var subQ0=sQuery(id+"F0.wireOp",EDGE,"E152");var subQ1=sQuery(id+"F0.wireOp",EDGE,"E37");var subQ2=makeQuery(id+"F0.imprint","INTERSECT",VERTEX,{"derivedFrom":[subQ1,subQ0]});Q60=makeQuery(id+"F0.imprint","IMPRINT",FACE,{"disambiguationData":[TD([[makeQuery(id+"F0.imprint","IMPRINT",EDGE,{"disambiguationData":[TD([[subQ2,-1.0]])],"derivedFrom":subQ1}),-1.0]])]});}
            var Q61;
            {var subQ0=sQuery(id+"F0.wireOp",EDGE,"E46");var subQ3=sQuery(id+"F0.wireOp",EDGE,"E37");var subQ4=makeQuery(id+"F0.imprint","INTERSECT",VERTEX,{"derivedFrom":[subQ3,subQ0]});Q61=makeQuery(id+"F0.imprint","IMPRINT",FACE,{"disambiguationData":[TD([[makeQuery(id+"F0.imprint","IMPRINT",EDGE,{"disambiguationData":[TD([[subQ4,-1.0]])],"derivedFrom":subQ3}),-1.0]])]});}
            var Q62;
            {var subQ0=sQuery(id+"F0.wireOp",EDGE,"E47");var subQ1=sQuery(id+"F0.wireOp",EDGE,"E33");var subQ2=makeQuery(id+"F0.imprint","INTERSECT",VERTEX,{"derivedFrom":[subQ1,subQ0]});Q62=makeQuery(id+"F0.imprint","IMPRINT",FACE,{"disambiguationData":[TD([[makeQuery(id+"F0.imprint","IMPRINT",EDGE,{"disambiguationData":[TD([[subQ2,-1.0]])],"derivedFrom":subQ1}),-1.0]])]});}
            var Q63;
            {var subQ0=sQuery(id+"F0.wireOp",EDGE,"E47");var subQ1=sQuery(id+"F0.wireOp",EDGE,"E35");var subQ2=makeQuery(id+"F0.imprint","INTERSECT",VERTEX,{"derivedFrom":[subQ1,subQ0]});Q63=makeQuery(id+"F0.imprint","IMPRINT",FACE,{"disambiguationData":[TD([[makeQuery(id+"F0.imprint","IMPRINT",EDGE,{"disambiguationData":[TD([[subQ2,-1.0]])],"derivedFrom":subQ1}),-1.0]])]});}
            var Q64;
            {var subQ0=sQuery(id+"F0.wireOp",EDGE,"E47");var subQ1=sQuery(id+"F0.wireOp",EDGE,"E37");var subQ2=makeQuery(id+"F0.imprint","INTERSECT",VERTEX,{"derivedFrom":[subQ1,subQ0]});Q64=makeQuery(id+"F0.imprint","IMPRINT",FACE,{"disambiguationData":[TD([[makeQuery(id+"F0.imprint","IMPRINT",EDGE,{"disambiguationData":[TD([[subQ2,-1.0]])],"derivedFrom":subQ1}),-1.0]])]});}
            var Q65;
            {var subQ0=sQuery(id+"F0.wireOp",EDGE,"E207");Q65=makeQuery(id+"F0.imprint","IMPRINT",FACE,{"disambiguationData":[TD([[makeQuery(id+"F0.imprint","IMPRINT",EDGE,{"derivedFrom":subQ0}),-1.0]])]});}
            var Q66;
            {var subQ0=sQuery(id+"F0.wireOp",EDGE,"E47");var subQ1=sQuery(id+"F0.wireOp",EDGE,"E29");var subQ2=makeQuery(id+"F0.imprint","INTERSECT",VERTEX,{"derivedFrom":[subQ1,subQ0]});Q66=makeQuery(id+"F0.imprint","IMPRINT",FACE,{"disambiguationData":[TD([[makeQuery(id+"F0.imprint","IMPRINT",EDGE,{"disambiguationData":[TD([[subQ2,-1.0]])],"derivedFrom":subQ1}),-1.0]])]});}
            var Q67;
            {var subQ0=sQuery(id+"F0.wireOp",EDGE,"E47");var subQ1=sQuery(id+"F0.wireOp",EDGE,"E29");var subQ2=makeQuery(id+"F0.imprint","INTERSECT",VERTEX,{"derivedFrom":[subQ1,subQ0]});Q67=makeQuery(id+"F0.imprint","IMPRINT",FACE,{"disambiguationData":[TD([[makeQuery(id+"F0.imprint","IMPRINT",EDGE,{"disambiguationData":[TD([[subQ2,-1.0]])],"derivedFrom":subQ1}),1.0]])]});}
            var Q68;
            {var subQ0=sQuery(id+"F0.wireOp",EDGE,"E174");Q68=makeQuery(id+"F0.imprint","IMPRINT",FACE,{"disambiguationData":[TD([[makeQuery(id+"F0.imprint","IMPRINT",EDGE,{"derivedFrom":subQ0}),-1.0]])]});}
            var Q69;
            {var subQ0=sQuery(id+"F0.wireOp",EDGE,"E196");Q69=makeQuery(id+"F0.imprint","IMPRINT",FACE,{"disambiguationData":[TD([[makeQuery(id+"F0.imprint","IMPRINT",EDGE,{"derivedFrom":subQ0}),1.0]])]});}
            var Q70;
            {var subQ0=sQuery(id+"F0.wireOp",EDGE,"E47");var subQ1=sQuery(id+"F0.wireOp",EDGE,"E39");var subQ2=makeQuery(id+"F0.imprint","INTERSECT",VERTEX,{"derivedFrom":[subQ1,subQ0]});Q70=makeQuery(id+"F0.imprint","IMPRINT",FACE,{"disambiguationData":[TD([[makeQuery(id+"F0.imprint","IMPRINT",EDGE,{"disambiguationData":[TD([[subQ2,-1.0]])],"derivedFrom":subQ1}),-1.0]])]});}
            var Q71;
            {var subQ0=sQuery(id+"F0.wireOp",EDGE,"E47");var subQ1=sQuery(id+"F0.wireOp",EDGE,"E31");var subQ2=makeQuery(id+"F0.imprint","INTERSECT",VERTEX,{"derivedFrom":[subQ1,subQ0]});Q71=makeQuery(id+"F0.imprint","IMPRINT",FACE,{"disambiguationData":[TD([[makeQuery(id+"F0.imprint","IMPRINT",EDGE,{"disambiguationData":[TD([[subQ2,-1.0]])],"derivedFrom":subQ1}),-1.0]])]});}
            var Q72;
            Q72=sQuery(id+"F0.wireOp",EDGE,"E47");
            var Q73;
            Q73=sQuery(id+"F0.wireOp",EDGE,"E149");
            var Q74;
            Q74=sQuery(id+"F0.wireOp",EDGE,"E152");
            var Q75;
            Q75=sQuery(id+"F0.wireOp",EDGE,"E208");
            var Q76;
            Q76=sQuery(id+"F0.wireOp",EDGE,"E173");
            var Q77;
            Q77=sQuery(id+"F0.wireOp",EDGE,"E206");
            var Q78;
            Q78=sQuery(id+"F0.wireOp",EDGE,"LkYlqQJV-c5Ik-aOkg-Fd5u-UOqOfWX4Qkif");
            var Q79;
            Q79=sQuery(id+"F0.wireOp",EDGE,"E172");
            var Q80;
            Q80=sQuery(id+"F0.wireOp",EDGE,"E174");
            var Q81;
            Q81=sQuery(id+"F0.wireOp",EDGE,"E175");
            var Q82;
            Q82=sQuery(id+"F0.wireOp",EDGE,"E202");
            var Q83;
            Q83=sQuery(id+"F0.wireOp",EDGE,"E200");
            var Q84;
            Q84=sQuery(id+"F0.wireOp",EDGE,"E197");
            var Q85;
            Q85=sQuery(id+"F0.wireOp",EDGE,"E196");
            var Q86;
            Q86=sQuery(id+"F0.wireOp",EDGE,"E198");
            var Q87;
            Q87=sQuery(id+"F0.wireOp",EDGE,"E201");
            var Q88;
            Q88=sQuery(id+"F0.wireOp",EDGE,"E204");
            var Q89;
            Q89=sQuery(id+"F0.wireOp",EDGE,"E203");
            var Q90;
            Q90=sQuery(id+"F0.wireOp",EDGE,"E46");
            var Q91;
            Q91=sQuery(id+"F0.wireOp",EDGE,"E205");
            extrude(context, id + "F1", {"entities" : qUnion([Q0, Q1, Q2, Q3, Q4, Q5, Q6, Q7, Q8, Q9, Q10, Q11, Q12, Q13, Q14, Q15, Q16, Q17, Q18, Q19, Q20, Q21, Q22, Q23, Q24, Q25, Q26, Q27, Q28, Q29, Q30, Q31, Q32, Q33, Q34, Q35, Q36, Q37, Q38, Q39, Q40, Q41, Q42, Q43, Q44, Q45, Q46, Q47, Q48, Q49, Q50, Q51, Q52, Q53, Q54, Q55, Q56, Q57, Q58, Q59, Q60, Q61, Q62, Q63, Q64, Q65, Q66, Q67, Q68, Q69, Q70, Q71]), "surfaceEntities" : qUnion([Q72, Q73, Q74, Q75, Q76, Q77, Q78, Q79, Q80, Q81, Q82, Q83, Q84, Q85, Q86, Q87, Q88, Q89, Q90, Q91]), "depth" : 3 * mm, "offsetDistance" : 25 * mm});
        }
        {
            var Q0;
            {var subQ0=sQuery(id+"F0.wireOp",EDGE,"E66");Q0=makeQuery(id+"F1.opExtrude","CAP_EDGE",EDGE,{"disambiguationData":[OSD([subQ0]),TDD([makeQuery(id+"F0.imprint","IMPRINT",EDGE,{"disambiguationData":[TD([[makeQuery(id+"F0.imprint","INTERSECT",VERTEX,{"derivedFrom":[subQ0,sQuery(id+"F0.wireOp",EDGE,"E129")]}),-1.0]])],"derivedFrom":subQ0})])],"isStart":false});}
            var Q1;
            Q1=makeQuery(id+"F1.opExtrude","CAP_EDGE",EDGE,{"disambiguationData":[OSD([sQuery(id+"F0.wireOp",EDGE,"E145")])],"isStart":false});
            var Q2;
            {var subQ0=sQuery(id+"F0.wireOp",EDGE,"E44");Q2=makeQuery(id+"F1.opExtrude","CAP_EDGE",EDGE,{"disambiguationData":[OSD([subQ0]),TDD([makeQuery(id+"F0.imprint","IMPRINT",EDGE,{"disambiguationData":[TD([[makeQuery(id+"F0.imprint","INTERSECT",VERTEX,{"derivedFrom":[subQ0,sQuery(id+"F0.wireOp",EDGE,"E129")]}),-1.0]])],"derivedFrom":subQ0})])],"isStart":false});}
            var Q3;
            Q3=makeQuery(id+"F1.opExtrude","CAP_EDGE",EDGE,{"disambiguationData":[OSD([sQuery(id+"F0.wireOp",EDGE,"E129")])],"isStart":false});
            var Q4;
            Q4=makeQuery(id+"F1.opExtrude","CAP_EDGE",EDGE,{"disambiguationData":[OSD([sQuery(id+"F0.wireOp",EDGE,"E74.0")])],"isStart":false});
            var Q5;
            Q5=makeQuery(id+"F1.opExtrude","CAP_EDGE",EDGE,{"disambiguationData":[OSD([sQuery(id+"F0.wireOp",EDGE,"E75.0")])],"isStart":false});
            var Q6;
            Q6=makeQuery(id+"F1.opExtrude","CAP_EDGE",EDGE,{"disambiguationData":[OSD([sQuery(id+"F0.wireOp",EDGE,"E70.0")])],"isStart":false});
            var Q7;
            Q7=makeQuery(id+"F1.opExtrude","CAP_EDGE",EDGE,{"disambiguationData":[OSD([sQuery(id+"F0.wireOp",EDGE,"E117")])],"isStart":false});
            var Q8;
            Q8=makeQuery(id+"F1.opExtrude","CAP_EDGE",EDGE,{"disambiguationData":[OSD([sQuery(id+"F0.wireOp",EDGE,"E71.0")])],"isStart":false});
            var Q9;
            Q9=makeQuery(id+"F1.opExtrude","CAP_EDGE",EDGE,{"disambiguationData":[OSD([sQuery(id+"F0.wireOp",EDGE,"E132")])],"isStart":false});
            var Q10;
            {var subQ0=sQuery(id+"F0.wireOp",EDGE,"E66");Q10=makeQuery(id+"F1.opExtrude","CAP_EDGE",EDGE,{"disambiguationData":[OSD([subQ0]),TDD([makeQuery(id+"F0.imprint","IMPRINT",EDGE,{"disambiguationData":[TD([[makeQuery(id+"F0.imprint","INTERSECT",VERTEX,{"derivedFrom":[subQ0,sQuery(id+"F0.wireOp",EDGE,"E67")]}),1.0]])],"derivedFrom":subQ0})])],"isStart":false});}
            var Q11;
            Q11=makeQuery(id+"F1.opExtrude","CAP_EDGE",EDGE,{"disambiguationData":[OSD([sQuery(id+"F0.wireOp",EDGE,"E67")])],"isStart":false});
            var Q12;
            Q12=makeQuery(id+"F1.opExtrude","CAP_EDGE",EDGE,{"disambiguationData":[OSD([sQuery(id+"F0.wireOp",EDGE,"E62")])],"isStart":false});
            var Q13;
            Q13=makeQuery(id+"F1.opExtrude","CAP_FACE",FACE,{"disambiguationData":[OSD([sQuery(id+"F0.wireOp",EDGE,"E27"),sQuery(id+"F0.wireOp",EDGE,"E42"),sQuery(id+"F0.wireOp",EDGE,"E43"),sQuery(id+"F0.wireOp",EDGE,"E44"),sQuery(id+"F0.wireOp",EDGE,"E45"),sQuery(id+"F0.wireOp",EDGE,"E46"),sQuery(id+"F0.wireOp",EDGE,"E48"),sQuery(id+"F0.wireOp",EDGE,"E49"),sQuery(id+"F0.wireOp",EDGE,"E51"),sQuery(id+"F0.wireOp",EDGE,"E52"),sQuery(id+"F0.wireOp",EDGE,"E54"),sQuery(id+"F0.wireOp",EDGE,"E55"),sQuery(id+"F0.wireOp",EDGE,"E57"),sQuery(id+"F0.wireOp",EDGE,"E59"),sQuery(id+"F0.wireOp",EDGE,"E60"),sQuery(id+"F0.wireOp",EDGE,"E62"),sQuery(id+"F0.wireOp",EDGE,"E63"),sQuery(id+"F0.wireOp",EDGE,"E66"),sQuery(id+"F0.wireOp",EDGE,"E67"),sQuery(id+"F0.wireOp",EDGE,"E68"),sQuery(id+"F0.wireOp",EDGE,"E69"),sQuery(id+"F0.wireOp",EDGE,"E70.0"),sQuery(id+"F0.wireOp",EDGE,"E71.0"),sQuery(id+"F0.wireOp",EDGE,"E72"),sQuery(id+"F0.wireOp",EDGE,"E73"),sQuery(id+"F0.wireOp",EDGE,"E74.0"),sQuery(id+"F0.wireOp",EDGE,"E75.0"),sQuery(id+"F0.wireOp",EDGE,"E80"),sQuery(id+"F0.wireOp",EDGE,"E81"),sQuery(id+"F0.wireOp",EDGE,"E114"),sQuery(id+"F0.wireOp",EDGE,"E115"),sQuery(id+"F0.wireOp",EDGE,"E116"),sQuery(id+"F0.wireOp",EDGE,"E117"),sQuery(id+"F0.wireOp",EDGE,"E118"),sQuery(id+"F0.wireOp",EDGE,"E119"),sQuery(id+"F0.wireOp",EDGE,"E120"),sQuery(id+"F0.wireOp",EDGE,"E121"),sQuery(id+"F0.wireOp",EDGE,"E122"),sQuery(id+"F0.wireOp",EDGE,"E123"),sQuery(id+"F0.wireOp",EDGE,"E124"),sQuery(id+"F0.wireOp",EDGE,"E128"),sQuery(id+"F0.wireOp",EDGE,"E129"),sQuery(id+"F0.wireOp",EDGE,"E132"),sQuery(id+"F0.wireOp",EDGE,"E134"),sQuery(id+"F0.wireOp",EDGE,"E136"),sQuery(id+"F0.wireOp",EDGE,"E139"),sQuery(id+"F0.wireOp",EDGE,"E140"),sQuery(id+"F0.wireOp",EDGE,"E142"),sQuery(id+"F0.wireOp",EDGE,"E145")])],"isStart":false});
            fillet(context, id + "F2", {"entities" : qUnion([Q0, Q1, Q2, Q3, Q4, Q5, Q6, Q7, Q8, Q9, Q10, Q11, Q12, Q13]), "radius" : 0.75 * mm, "rho" : 0.5, "crossSection" : FilletCrossSection.CONIC, "allowEdgeOverflow" : false});
        }
    });
